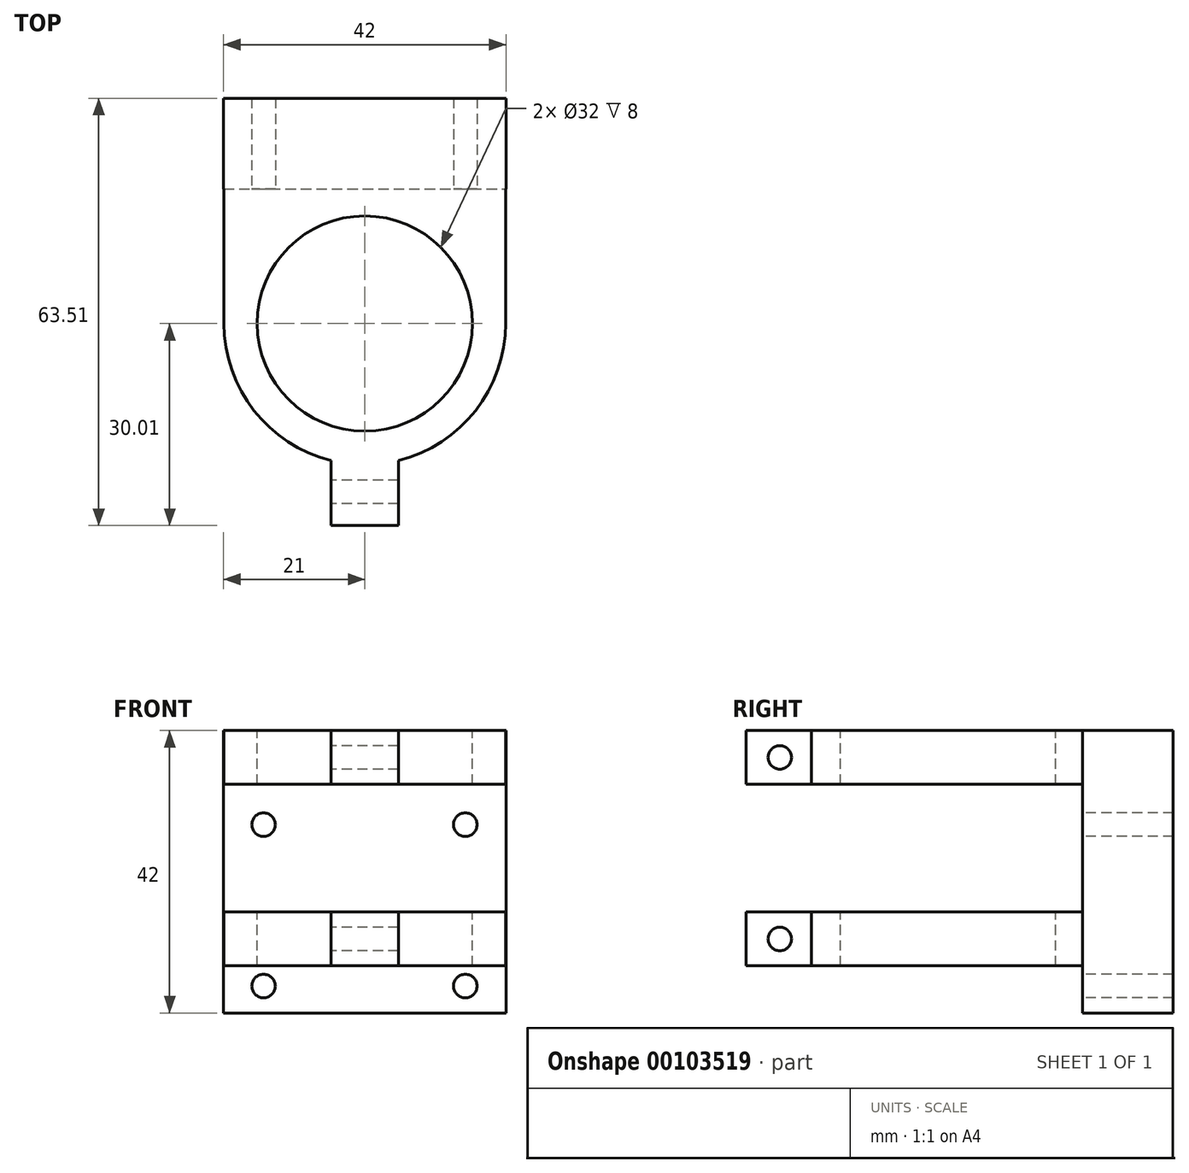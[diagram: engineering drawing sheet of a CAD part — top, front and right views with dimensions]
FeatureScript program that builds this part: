
annotation { "Feature Type Name" : "Feature", "Feature Type Description" : "" }
export const myFeature = defineFeature(function(context is Context, id is Id, definition is map)
    precondition{}
    {
        {
            var Q0;
            Q0=qCreatedBy(makeId("Top.planeOp"),FACE);
            var sketch = newSketch(context, id + "F0", { "sketchPlane" : qUnion([Q0])});
            skLineSegment(sketch, "E0.bottom", {"start": v(0, 0) * mm, "end": v(42, 0) * mm});
            skLineSegment(sketch, "E0.top", {"start": v(0, 10) * mm, "end": v(42, 10) * mm});
            skLineSegment(sketch, "E0.left", {"start": v(0, 0) * mm, "end": v(0, 10) * mm});
            skLineSegment(sketch, "E0.right", {"start": v(42, 0) * mm, "end": v(42, 10) * mm});
            skLineSegment(sketch, "E1.top", {"start": v(0, 13.5) * mm, "end": v(42, 13.5) * mm});
            skLineSegment(sketch, "E1.left", {"start": v(0, 10) * mm, "end": v(0, 13.5) * mm});
            skLineSegment(sketch, "E1.right", {"start": v(42, 10) * mm, "end": v(42, 13.5) * mm});
            skSolve(sketch);
        }
        {
            var Q0;
            Q0 = qSketchRegion(id + "F0", true);
            extrude(context, id + "F1", {"entities" : qUnion([Q0]), "offsetDistance" : 25 * mm, "depth" : 42 * mm});
        }
        {
            var Q0;
            Q0=makeQuery(id+"F1.opExtrude","SWEPT_FACE",FACE,{"disambiguationData":[OSD([sQuery(id+"F0.wireOp",EDGE,"E0.bottom")])]});
            var sketch = newSketch(context, id + "F2", { "sketchPlane" : qUnion([Q0])});
            skLineSegment(sketch, "E2", {"start": v(-0.06, 16) * mm, "end": v(42, 16) * mm, "construction": true});
            skCircle(sketch, "E3", {"center": v(5.94, 28) * mm, "radius": 1.75 * mm});
            skCircle(sketch, "E4.MirrorC", {"center": v(5.94, 4) * mm, "radius": 1.75 * mm});
            skLineSegment(sketch, "E5", {"start": v(20.94, 16) * mm, "end": v(20.94, 40.65) * mm, "construction": true});
            skCircle(sketch, "E6.MirrorC", {"center": v(35.94, 4) * mm, "radius": 1.75 * mm});
            skCircle(sketch, "E7.MirrorC", {"center": v(35.94, 28) * mm, "radius": 1.75 * mm});
            skSolve(sketch);
        }
        {
            var Q0;
            Q0 = qSketchRegion(id + "F2", true);
            extrude(context, id + "F3", {"entities" : qUnion([Q0]), "operationType" : NewBodyOperationType.REMOVE, "oppositeDirection" : true, "depth" : 25 * mm});
        }
        {
            var Q0;
            Q0=makeQuery(id+"F1.opExtrude","CAP_FACE",FACE,{"disambiguationData":[OSD([sQuery(id+"F0.wireOp",EDGE,"E0.bottom"),sQuery(id+"F0.wireOp",EDGE,"E0.top"),sQuery(id+"F0.wireOp",EDGE,"E0.left"),sQuery(id+"F0.wireOp",EDGE,"E0.right"),sQuery(id+"F0.wireOp",EDGE,"E1.top"),sQuery(id+"F0.wireOp",EDGE,"E1.left"),sQuery(id+"F0.wireOp",EDGE,"E1.right")])],"isStart":false});
            var sketch = newSketch(context, id + "F4", { "sketchPlane" : qUnion([Q0])});
            skLineSegment(sketch, "E8", {"start": v(42, 13.5) * mm, "end": v(42, -15.53) * mm, "construction": true});
            skLineSegment(sketch, "E9.bottom", {"start": v(17.43, 0) * mm, "end": v(24.57, 0) * mm, "construction": true});
            skLineSegment(sketch, "E9.top", {"start": v(17.43, -4) * mm, "end": v(24.57, -4) * mm, "construction": true});
            skLineSegment(sketch, "E9.left", {"start": v(24.57, 0) * mm, "end": v(24.57, -4) * mm, "construction": true});
            skLineSegment(sketch, "E9.right", {"start": v(17.43, 0) * mm, "end": v(17.43, -4) * mm, "construction": true});
            skCircle(sketch, "E10", {"center": v(21, -20) * mm, "radius": 16 * mm});
            skPoint(sketch, "E11", {"position": v(21, -4) * mm});
            skCircle(sketch, "E12", {"center": v(21, -20) * mm, "radius": 20.94 * mm});
            skLineSegment(sketch, "E13.bottom", {"start": v(20, -23.35) * mm, "end": v(22, -23.35) * mm});
            skLineSegment(sketch, "E13.top", {"start": v(20, -50.01) * mm, "end": v(22, -50.01) * mm});
            skLineSegment(sketch, "E13.left", {"start": v(20, -23.35) * mm, "end": v(20, -50.01) * mm});
            skLineSegment(sketch, "E13.right", {"start": v(22, -23.35) * mm, "end": v(22, -50.01) * mm});
            skLineSegment(sketch, "E14.bottom", {"start": v(16, -21.5) * mm, "end": v(26, -21.5) * mm});
            skLineSegment(sketch, "E14.top", {"start": v(16, -50.01) * mm, "end": v(26, -50.01) * mm});
            skLineSegment(sketch, "E14.left", {"start": v(16, -21.5) * mm, "end": v(16, -50.01) * mm});
            skLineSegment(sketch, "E14.right", {"start": v(26, -21.5) * mm, "end": v(26, -50.01) * mm});
            skPoint(sketch, "E15", {"position": v(21, -21.5) * mm});
            skCircle(sketch, "E16", {"center": v(21, -20) * mm, "radius": 14.5 * mm});
            skCircle(sketch, "E17", {"center": v(21, -20) * mm, "radius": 9.5 * mm});
            skLineSegment(sketch, "E18", {"start": v(0.06, -20) * mm, "end": v(0.06, 0.3) * mm});
            skLineSegment(sketch, "E19", {"start": v(0.06, -20) * mm, "end": v(41.94, -20) * mm, "construction": true});
            skLineSegment(sketch, "E20", {"start": v(14.78, 0) * mm, "end": v(-0.86, 0) * mm});
            skLineSegment(sketch, "E21", {"start": v(21, 0) * mm, "end": v(21, -12.43) * mm, "construction": true});
            skLineSegment(sketch, "E22.MirrorCS", {"start": v(41.94, -20) * mm, "end": v(41.94, 0.3) * mm});
            skLineSegment(sketch, "E23.MirrorCS", {"start": v(27.22, 0) * mm, "end": v(42.86, 0) * mm});
            skSolve(sketch);
        }
        {
            var Q0;
            {var subQ5=sQuery(id+"F4.wireOp",EDGE,"E14.left");var subQ7=sQuery(id+"F4.wireOp",EDGE,"E10");var subQ8=makeQuery(id+"F4.imprint","INTERSECT",VERTEX,{"derivedFrom":[subQ7,subQ5]});Q0=makeQuery(id+"F4.imprint","IMPRINT",FACE,{"disambiguationData":[TD([[makeQuery(id+"F4.imprint","IMPRINT",EDGE,{"disambiguationData":[TD([[subQ8,1.0]])],"derivedFrom":subQ7}),-1.0]])]});}
            var Q1;
            {var subQ0=sQuery(id+"F4.wireOp",EDGE,"E13.right");var subQ1=sQuery(id+"F4.wireOp",EDGE,"E10");var subQ2=makeQuery(id+"F4.imprint","INTERSECT",VERTEX,{"derivedFrom":[subQ1,subQ0]});Q1=makeQuery(id+"F4.imprint","IMPRINT",FACE,{"disambiguationData":[TD([[makeQuery(id+"F4.imprint","IMPRINT",EDGE,{"disambiguationData":[TD([[subQ2,-1.0]])],"derivedFrom":subQ1}),-1.0]])]});}
            var Q2;
            {var subQ0=sQuery(id+"F4.wireOp",EDGE,"E14.right");var subQ1=sQuery(id+"F4.wireOp",EDGE,"E12");var subQ2=makeQuery(id+"F4.imprint","INTERSECT",VERTEX,{"derivedFrom":[subQ1,subQ0]});Q2=makeQuery(id+"F4.imprint","IMPRINT",FACE,{"disambiguationData":[TD([[makeQuery(id+"F4.imprint","IMPRINT",EDGE,{"disambiguationData":[TD([[subQ2,1.0]])],"derivedFrom":subQ1}),-1.0]])]});}
            var Q3;
            {var subQ0=sQuery(id+"F4.wireOp",EDGE,"E14.left");var subQ1=sQuery(id+"F4.wireOp",EDGE,"E12");var subQ2=makeQuery(id+"F4.imprint","INTERSECT",VERTEX,{"derivedFrom":[subQ1,subQ0]});Q3=makeQuery(id+"F4.imprint","IMPRINT",FACE,{"disambiguationData":[TD([[makeQuery(id+"F4.imprint","IMPRINT",EDGE,{"disambiguationData":[TD([[subQ2,-1.0]])],"derivedFrom":subQ1}),-1.0]])]});}
            var Q4;
            {var subQ0=sQuery(id+"F4.wireOp",EDGE,"E13.left");var subQ1=sQuery(id+"F4.wireOp",EDGE,"E10");var subQ2=makeQuery(id+"F4.imprint","INTERSECT",VERTEX,{"derivedFrom":[subQ1,subQ0]});Q4=makeQuery(id+"F4.imprint","IMPRINT",FACE,{"disambiguationData":[TD([[makeQuery(id+"F4.imprint","IMPRINT",EDGE,{"disambiguationData":[TD([[subQ2,1.0]])],"derivedFrom":subQ1}),-1.0]])]});}
            var Q5;
            {var subQ0=sQuery(id+"F4.wireOp",EDGE,"E13.left");var subQ1=sQuery(id+"F4.wireOp",EDGE,"E10");var subQ2=makeQuery(id+"F4.imprint","INTERSECT",VERTEX,{"derivedFrom":[subQ1,subQ0]});Q5=makeQuery(id+"F4.imprint","IMPRINT",FACE,{"disambiguationData":[TD([[makeQuery(id+"F4.imprint","IMPRINT",EDGE,{"disambiguationData":[TD([[subQ2,-1.0]])],"derivedFrom":subQ1}),-1.0]])]});}
            var Q6;
            {var subQ0=sQuery(id+"F4.wireOp",EDGE,"E13.left");var subQ1=sQuery(id+"F4.wireOp",EDGE,"E12");var subQ2=makeQuery(id+"F4.imprint","INTERSECT",VERTEX,{"derivedFrom":[subQ1,subQ0]});Q6=makeQuery(id+"F4.imprint","IMPRINT",FACE,{"disambiguationData":[TD([[makeQuery(id+"F4.imprint","IMPRINT",EDGE,{"disambiguationData":[TD([[subQ2,-1.0]])],"derivedFrom":subQ1}),-1.0]])]});}
            var Q7;
            {var subQ0=sQuery(id+"F4.wireOp",EDGE,"E18");var subQ1=sQuery(id+"F4.wireOp",EDGE,"E12");var subQ2=makeQuery(id+"F4.imprint","INTERSECT",VERTEX,{"derivedFrom":[subQ1,subQ0]});Q7=makeQuery(id+"F4.imprint","IMPRINT",FACE,{"disambiguationData":[TD([[makeQuery(id+"F4.imprint","IMPRINT",EDGE,{"disambiguationData":[TD([[subQ2,-1.0]])],"derivedFrom":subQ0}),-1.0]])]});}
            var Q8;
            {var subQ0=sQuery(id+"F4.wireOp",EDGE,"E22.MirrorCS");var subQ1=sQuery(id+"F4.wireOp",EDGE,"E12");var subQ2=makeQuery(id+"F4.imprint","INTERSECT",VERTEX,{"derivedFrom":[subQ1,subQ0]});Q8=makeQuery(id+"F4.imprint","IMPRINT",FACE,{"disambiguationData":[TD([[makeQuery(id+"F4.imprint","IMPRINT",EDGE,{"disambiguationData":[TD([[subQ2,-1.0]])],"derivedFrom":subQ0}),1.0]])]});}
            extrude(context, id + "F5", {"entities" : qUnion([Q0, Q1, Q2, Q3, Q4, Q5, Q6, Q7, Q8]), "operationType" : NewBodyOperationType.ADD, "oppositeDirection" : true, "offsetDistance" : 25 * mm, "depth" : 8 * mm});
        }
        {
            var Q0;
            {var subQ5=sQuery(id+"F4.wireOp",EDGE,"E14.left");var subQ8=sQuery(id+"F4.wireOp",EDGE,"E10");var subQ9=makeQuery(id+"F4.imprint","INTERSECT",VERTEX,{"derivedFrom":[subQ8,subQ5]});Q0=makeQuery(id+"F4.imprint","IMPRINT",FACE,{"disambiguationData":[TD([[makeQuery(id+"F4.imprint","IMPRINT",EDGE,{"disambiguationData":[TD([[subQ9,1.0]])],"derivedFrom":subQ8}),-1.0]])]});}
            var Q1;
            {var subQ0=sQuery(id+"F4.wireOp",EDGE,"E13.left");var subQ1=sQuery(id+"F4.wireOp",EDGE,"E10");var subQ2=makeQuery(id+"F4.imprint","INTERSECT",VERTEX,{"derivedFrom":[subQ1,subQ0]});Q1=makeQuery(id+"F4.imprint","IMPRINT",FACE,{"disambiguationData":[TD([[makeQuery(id+"F4.imprint","IMPRINT",EDGE,{"disambiguationData":[TD([[subQ2,1.0]])],"derivedFrom":subQ1}),-1.0]])]});}
            var Q2;
            {var subQ0=sQuery(id+"F4.wireOp",EDGE,"E14.left");var subQ1=sQuery(id+"F4.wireOp",EDGE,"E12");var subQ2=makeQuery(id+"F4.imprint","INTERSECT",VERTEX,{"derivedFrom":[subQ1,subQ0]});Q2=makeQuery(id+"F4.imprint","IMPRINT",FACE,{"disambiguationData":[TD([[makeQuery(id+"F4.imprint","IMPRINT",EDGE,{"disambiguationData":[TD([[subQ2,-1.0]])],"derivedFrom":subQ1}),-1.0]])]});}
            var Q3;
            {var subQ0=sQuery(id+"F4.wireOp",EDGE,"E14.right");var subQ1=sQuery(id+"F4.wireOp",EDGE,"E12");var subQ2=makeQuery(id+"F4.imprint","INTERSECT",VERTEX,{"derivedFrom":[subQ1,subQ0]});Q3=makeQuery(id+"F4.imprint","IMPRINT",FACE,{"disambiguationData":[TD([[makeQuery(id+"F4.imprint","IMPRINT",EDGE,{"disambiguationData":[TD([[subQ2,1.0]])],"derivedFrom":subQ1}),-1.0]])]});}
            var Q4;
            {var subQ0=sQuery(id+"F4.wireOp",EDGE,"E13.right");var subQ1=sQuery(id+"F4.wireOp",EDGE,"E10");var subQ2=makeQuery(id+"F4.imprint","INTERSECT",VERTEX,{"derivedFrom":[subQ1,subQ0]});Q4=makeQuery(id+"F4.imprint","IMPRINT",FACE,{"disambiguationData":[TD([[makeQuery(id+"F4.imprint","IMPRINT",EDGE,{"disambiguationData":[TD([[subQ2,-1.0]])],"derivedFrom":subQ1}),-1.0]])]});}
            var Q5;
            {var subQ0=sQuery(id+"F4.wireOp",EDGE,"E13.left");var subQ1=sQuery(id+"F4.wireOp",EDGE,"E12");var subQ2=makeQuery(id+"F4.imprint","INTERSECT",VERTEX,{"derivedFrom":[subQ1,subQ0]});Q5=makeQuery(id+"F4.imprint","IMPRINT",FACE,{"disambiguationData":[TD([[makeQuery(id+"F4.imprint","IMPRINT",EDGE,{"disambiguationData":[TD([[subQ2,-1.0]])],"derivedFrom":subQ1}),-1.0]])]});}
            var Q6;
            {var subQ0=sQuery(id+"F4.wireOp",EDGE,"E13.left");var subQ1=sQuery(id+"F4.wireOp",EDGE,"E10");var subQ2=makeQuery(id+"F4.imprint","INTERSECT",VERTEX,{"derivedFrom":[subQ1,subQ0]});Q6=makeQuery(id+"F4.imprint","IMPRINT",FACE,{"disambiguationData":[TD([[makeQuery(id+"F4.imprint","IMPRINT",EDGE,{"disambiguationData":[TD([[subQ2,-1.0]])],"derivedFrom":subQ1}),-1.0]])]});}
            var Q7;
            {var subQ0=sQuery(id+"F4.wireOp",EDGE,"E18");var subQ1=sQuery(id+"F4.wireOp",EDGE,"E12");var subQ2=makeQuery(id+"F4.imprint","INTERSECT",VERTEX,{"derivedFrom":[subQ1,subQ0]});Q7=makeQuery(id+"F4.imprint","IMPRINT",FACE,{"disambiguationData":[TD([[makeQuery(id+"F4.imprint","IMPRINT",EDGE,{"disambiguationData":[TD([[subQ2,-1.0]])],"derivedFrom":subQ0}),-1.0]])]});}
            var Q8;
            {var subQ0=sQuery(id+"F4.wireOp",EDGE,"E22.MirrorCS");var subQ1=sQuery(id+"F4.wireOp",EDGE,"E12");var subQ2=makeQuery(id+"F4.imprint","INTERSECT",VERTEX,{"derivedFrom":[subQ1,subQ0]});Q8=makeQuery(id+"F4.imprint","IMPRINT",FACE,{"disambiguationData":[TD([[makeQuery(id+"F4.imprint","IMPRINT",EDGE,{"disambiguationData":[TD([[subQ2,-1.0]])],"derivedFrom":subQ0}),1.0]])]});}
            extrude(context, id + "F6", {"entities" : qUnion([Q0, Q1, Q2, Q3, Q4, Q5, Q6, Q7, Q8]), "operationType" : NewBodyOperationType.ADD, "oppositeDirection" : true, "offsetDistance" : 25 * mm, "depth" : 35 * mm, "hasSecondDirection" : true, "secondDirectionOppositeDirection" : true, "secondDirectionDepth" : 27 * mm});
        }
        {
            var Q0;
            Q0=makeQuery(id+"F5.opExtrude","SWEPT_FACE",FACE,{"disambiguationData":[OSD([sQuery(id+"F4.wireOp",EDGE,"E14.left")])]});
            var sketch = newSketch(context, id + "F7", { "sketchPlane" : qUnion([Q0])});
            skCircle(sketch, "E24", {"center": v(45.01, 38) * mm, "radius": 1.75 * mm});
            skLineSegment(sketch, "E25.0.0", {"start": v(50.01, 15) * mm, "end": v(40.34, 15) * mm, "construction": true});
            skLineSegment(sketch, "E25.0.1", {"start": v(40.34, 15) * mm, "end": v(40.34, 7) * mm, "construction": true});
            skLineSegment(sketch, "E25.0.2", {"start": v(40.34, 7) * mm, "end": v(50.01, 7) * mm, "construction": true});
            skLineSegment(sketch, "E25.0.3", {"start": v(50.01, 7) * mm, "end": v(50.01, 15) * mm, "construction": true});
            skLineSegment(sketch, "E26", {"start": v(50.01, 34) * mm, "end": v(50.01, 15) * mm, "construction": true});
            skLineSegment(sketch, "E27", {"start": v(50.01, 24.5) * mm, "end": v(42.59, 24.5) * mm, "construction": true});
            skPoint(sketch, "E27.endSnap0", {"position": v(50.01, 24.5) * mm});
            skCircle(sketch, "E28.MirrorC", {"center": v(45.01, 11) * mm, "radius": 1.75 * mm});
            skSolve(sketch);
        }
        {
            var Q0;
            Q0 = qSketchRegion(id + "F7", true);
            extrude(context, id + "F8", {"entities" : qUnion([Q0]), "operationType" : NewBodyOperationType.REMOVE, "oppositeDirection" : true, "depth" : 25 * mm});
        }
        {
            var Q0;
            Q0=makeQuery(id+"F5.opExtrude","CAP_FACE",FACE,{"disambiguationData":[OSD([sQuery(id+"F0.wireOp",EDGE,"E0.bottom"),sQuery(id+"F4.wireOp",EDGE,"E10"),sQuery(id+"F4.wireOp",EDGE,"E12"),sQuery(id+"F4.wireOp",EDGE,"E14.top"),sQuery(id+"F4.wireOp",EDGE,"E14.left"),sQuery(id+"F4.wireOp",EDGE,"E14.right")])],"isStart":false});
            cPlane(context, id + "F9", {"entities" : qUnion([Q0]), "cplaneType" : CPlaneType.OFFSET, "offset" : 0 * mm, "width" : 150 * mm, "height" : 150 * mm});
        }
        {
            var Q0;
            Q0=makeQuery(id+"F6.opExtrude","CAP_FACE",FACE,{"disambiguationData":[OSD([sQuery(id+"F0.wireOp",EDGE,"E0.bottom"),sQuery(id+"F4.wireOp",EDGE,"E10"),sQuery(id+"F4.wireOp",EDGE,"E12"),sQuery(id+"F4.wireOp",EDGE,"E14.top"),sQuery(id+"F4.wireOp",EDGE,"E14.left"),sQuery(id+"F4.wireOp",EDGE,"E14.right")])],"isStart":true});
            cPlane(context, id + "F10", {"entities" : qUnion([Q0]), "cplaneType" : CPlaneType.OFFSET, "offset" : 0 * mm, "width" : 150 * mm, "height" : 150 * mm});
        }
        {
            var Q0;
            Q0=makeQuery(id+"F6.opExtrude","CAP_FACE",FACE,{"disambiguationData":[OSD([sQuery(id+"F0.wireOp",EDGE,"E0.bottom"),sQuery(id+"F4.wireOp",EDGE,"E10"),sQuery(id+"F4.wireOp",EDGE,"E12"),sQuery(id+"F4.wireOp",EDGE,"E14.top"),sQuery(id+"F4.wireOp",EDGE,"E14.left"),sQuery(id+"F4.wireOp",EDGE,"E14.right")])],"isStart":false});
            cPlane(context, id + "F11", {"entities" : qUnion([Q0]), "cplaneType" : CPlaneType.OFFSET, "offset" : 0 * mm, "width" : 150 * mm, "height" : 150 * mm});
        }
    });
